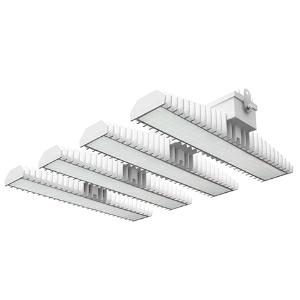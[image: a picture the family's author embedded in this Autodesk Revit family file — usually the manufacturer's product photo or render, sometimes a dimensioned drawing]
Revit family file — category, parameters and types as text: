
# Revit family: 3f_filippi_-_3f_lem_ampio_3f_filippi_-_59160_a0812_-_3f_lem_4_led_200-865_cr_ampio___vs_fc1b
name_source: partatom
category: Lighting Fixtures
units: mm (PartAtom-declared; Revit-internal decimal feet)

## family parameters
Cut with Voids When Loaded = No
Host = Face
Light Source = No
Part Type = Normal
Room Calculation Point = No
Round Connector Dimension = Use Diameter
Shared = No

## types (1)
- 3F Filippi - 3F LEM Ampio (1 x LED, 26607 lm, 218 W, 6500 K)
    Apparent Load = 218 VA
    Approval mark = CE
    CIE Flux Codes = 67 90 97 100 100
    Color Rendering = 80
    Color Temperature = 6500 K
    Control Gear = Electronic ballast
    Default Elevation = 1800 mm
    Description = Industrial luminaire with high light output and high luminous efficiency designed with the most innovative technologies for environments with temperature up to 55°C.

ILLUMINOTECHNICAL
Luminous efficiency 100% (DLOR 98%, ULOR 2%).
Initial luminous flux of the luminaire 26607 lm.
Direct symmetric wide distribution: the illuminated area has a rectangular shape.
Installation Interdistance Transv.D = 1.24 x hu - Long.D = 1.20 x hu.
Tabular UGR (CIE 117 - 4H-8H; S=0.25H; 70/50/20): RUG 22.8 - 22.9.
Beam angle: 82° - 83°.
Luminous efficacy 122 lm/W.
Lifetime (L93/B10): 30000 h. (tq+25°C)
Lifetime (L90/B10): 50000 h. (tq+25°C)
Lifetime (L85/B10): 80000 h. (tq+25°C)
Lifetime (L80/B10): 100000 h. (tq+25°C)
Lifetime (L85/B10): 50000 h. (tq+55°C)
Sudden decreased luminous flux after 50000 hours: 0% (C0).
Photobiological safety in compliance with IEC/TR 62778: RG0 risk exempt, (IEC 62471).
In compliance with IEC/EN 62722-2-1 - IEC/EN 62717 standards.

SOURCE
4 Mid-Power linear LED modules 50W/865.
Energy efficiency class (UE 2019/2020 - UE 2019/2015): C.
CIE 13.3 Colour rendering index: CRI >80 (R9 <50%).
IES TM-30 Fidelity Index: Rf = 84 Rg = 95.
CCT nominal colour temperature 6500 K.
Colour initial tolerance (MacAdam): SDCM 3.

MECHANICAL
Passive modular heatsinks in die-casted aluminium, painted in white colour.
To optimize the thermal management of the LED module, the heatsinks are oversized and provided with self-cleaning of cooling fins.
Wiring body in aluminium and galvanised steel anchored solidly to the sinks and thermally separated.
3F Lens lenses with high luminous efficiency, transparent methacrylate (PMMA), fixed to the LED modules.
Fixing brackets in stainless steel.
Luminaire with limited surface temperature. - D - (EN 60598-2-24)
Dimensions: 757x542 mm, height 133 mm. Weight 19.12 kg.
IP65 protection degree.
Mechanical strength to impacts IK06 (1 joule).
Glow-wire test resistance 650°C.

ELECTRICAL
Halogen Free electronic wiring 230V-50/60Hz, power factor 0.97, THD <25%, constant output current, class I, 2 driver.
Power of the luminaire 218 W.
ENEC - CE.
SAFE FLICKER: PstLM=<1 and SVM=<0.4 (IEC TR 61547-1 and IEC TR 63158), to ensure a more comfortable and safe light.
Luminaire compliant with EN 60598-2-22 for power supply from a centralised emergency system CPSS (Central Power Supply System), not incorporated in the luminaire - high risk areas excluded. The default power and flux are 100% in AC and 100% in DC.
Ambient temperature from -30°C to +55°C.
Temperature class T6 max 85°C.
Quick connection via M20 3P connector with 9-13 mm tightening range.
Power unit positioned on a separate compartment by the LED module to ensure optimum temperatures of cabling components, to be inspectable and maintainable.
Relative humidity UR: <85%.

INSTALLATION
Ceiling / Suspended / Wall.
All accessories dedicated to this product are available on the Catalog and on our website www.3F-Filippi.com.

ACCESSORIES
A0812 - Anti-glare microprismatic VS moulded glass, tempered, not flammable, with sealing gasket.
One required for each light module. The pack contains 10 pieces.

APPLICATIONS
In commercial environments, exhibition and industrial areas, stores, open areas.
Applications with high ambient temperature up to 55°C.
Environments in which it is necessary a total protection against falling fragments (eg environments with foodstuffs or machines with moving parts or with extreme temperature changes), use luminaires with polycarbonate lenses.

WARNING
Fixture not suitable for cold stores with an ambient temperature <0°C and/or relative humidity >85%.
Luminaire designed for disposal/recycling at end-of-life.
Replaceable (LED only) light source by a professional. Replaceable control gear by a professional.
    Height = 133 mm  [stored 0.436352 ft]
    Lamp = 1 x LED
    Lamp Light Flux = 26607 lm
    Lamp Power = 218 W
    Lamp count = 1
    Length = 757 mm
    Lifetime = 50000 h
    Luminous efficacy = 122 lm/W
    Manufacturer = 3F Filippi
    ModVariant = No
    Model = 3F Filippi - 59160+A0812 - 3F LEM 4 LED 200-865 CR AMPIO + VS
    Mounting Place = Ceiling
    Mounting Type = Pendant
    Number of Poles = 1
    OnlyDefault = Yes
    Power Factor = 1
    Product Name = 3F Filippi - 3F LEM Ampio
    Product group = pendant luminaire
    ProductGroupID = 9
    Protection Class = Protection class I
    Protection Degree = IP 65
    RLX_Detail_Level = 1
    RLX_Emergency_Light_Flux = 0 lm
    RLX_Emergency_Type = 0
    RLX_Emergency_Type_DB = No
    RlxData = <blob elided: 120409 chars, md5=08489ab3>
    Socket = socket
    Standby Power = 0 W
    System Light Flux = 26607 lm
    System Power = 218 W
    Type Comments = Product without accessories
    Type Image = 3f_filippi_-_lem_4__a0812.jpg
    URL = http://relux.com
    VarID = ---
    Voltage = 0 V
    Weight = 0.00 kg
    Width = 542 mm

note: [stored X ft] marks values corroborated as IEEE doubles in the binary element streams (Revit-internal decimal feet)

## geometry (parser evidence)
native form markers: Blend x4, Sweep x11
no freeform markers — native parametric forms only
